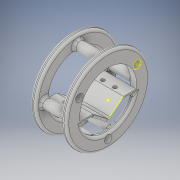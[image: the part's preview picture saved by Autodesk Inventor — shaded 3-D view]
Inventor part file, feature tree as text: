
AUTODESK INVENTOR PART (.ipt)
format: ipt  version: 2019 (Build 230136000, 136)  size: 677,376 bytes
history: native  units: in
note: dims shown in document units (in); Inventor stores cm internally (conversion verified against a paired STEP export)
features: fillet x10, sketch x9, extrude x7, mirror x2, projected_geometry x2, plane x1, pattern_circular x1
ambient origin geometry x8: Origin, YZ Plane, XZ Plane, XY Plane, X Axis, Y Axis, Z Axis, Center Point
bodies: Solid1 (feature_tree)
feature tree (32):
  extrude  "Extrusion1"  Depth=0.4331in
  extrude  "Extrusion2"  Depth=0.5118in
  mirror  "Mirror1"
  extrude  "Extrusion3"  Depth=0.3603in
  plane  "Work Plane1"
  extrude  "Extrusion4"  Depth=0.1181in
  extrude  "Extrusion5"  Depth=1.1811in TaperAngle=0.0deg
  pattern_circular  "Circular Pattern1"  Count=3  [1 undecoded]
  extrude  "Extrusion6"  Depth=0.1969in TaperAngle=0.0deg
  extrude  "Extrusion7"  Depth=0.2441in
  mirror  "Mirror2"
  sketch  "Sketch12"  dims[d48=0.1969in d49=0.0in]
  sketch  "Sketch14"  dims[d50=0.4724in d51=0.0787in d52=90.0deg d53=0.122in d55=0.0787in d56=0.0787in d57=0.0591in d58=0.0787in d59=0.0787in d60=0.0787in d61=0.0787in d62=0.0787in d63=0.0787in d64=0.1969in d65=0.0591in]
  fillet  "Fillet2"  Radius=0.7874in
  fillet  "Fillet3"  Radius=1.1811in
  fillet  "Fillet4"  Radius=2.1654in
  fillet  "Fillet5"  Radius=0.2756in
  fillet  "Fillet6"  Radius=0.1969in
  fillet  "Fillet7"  Radius=0.1969in
  fillet  "Fillet8"  Radius=0.2756in
  fillet  "Fillet9"  Radius=0.2756in
  fillet  "Fillet10"  Radius=1.1811in
  fillet  "Fillet11"  Radius=0.122in
  sketch  "Sketch2"  dims[d4=2.7165in d5=0.4331in]
  sketch  "Sketch4"  dims[d6=0.1969in d7=0.0in d16=0.5118in]
  sketch  "Sketch5"  dims[d17=0.5118in d18=0.3603in]
  projected_geometry  "Projected Loop1"
  sketch  "Sketch6"  dims[d20=0.1181in d21=0.1181in]
  projected_geometry  "Projected Loop2"
  sketch  "Sketch9"  dims[d22=180.0deg d23=1.1811in d24=0.0in d25=1.1811in d26=0.0in]
  sketch  "Sketch10"  dims[d27=-1.1811in d28=0.1969in d29=0.0in]
  sketch  "Sketch11"  dims[d32=2.1654in d33=0.2441in d34=0.7874in d35=0.0in d36=1.1811in d37=360.0deg d39=2.1654in d40=0.2756in d41=0.1969in d42=0.1969in d43=0.2756in d44=0.2756in d45=1.1811in d46=0.0in d47=0.122in]
note: 1 required parameter value undecoded (feature->parameter linkage not recoverable at this tier; creation-order binding heuristic only, values carry confidence <= 0.55)
